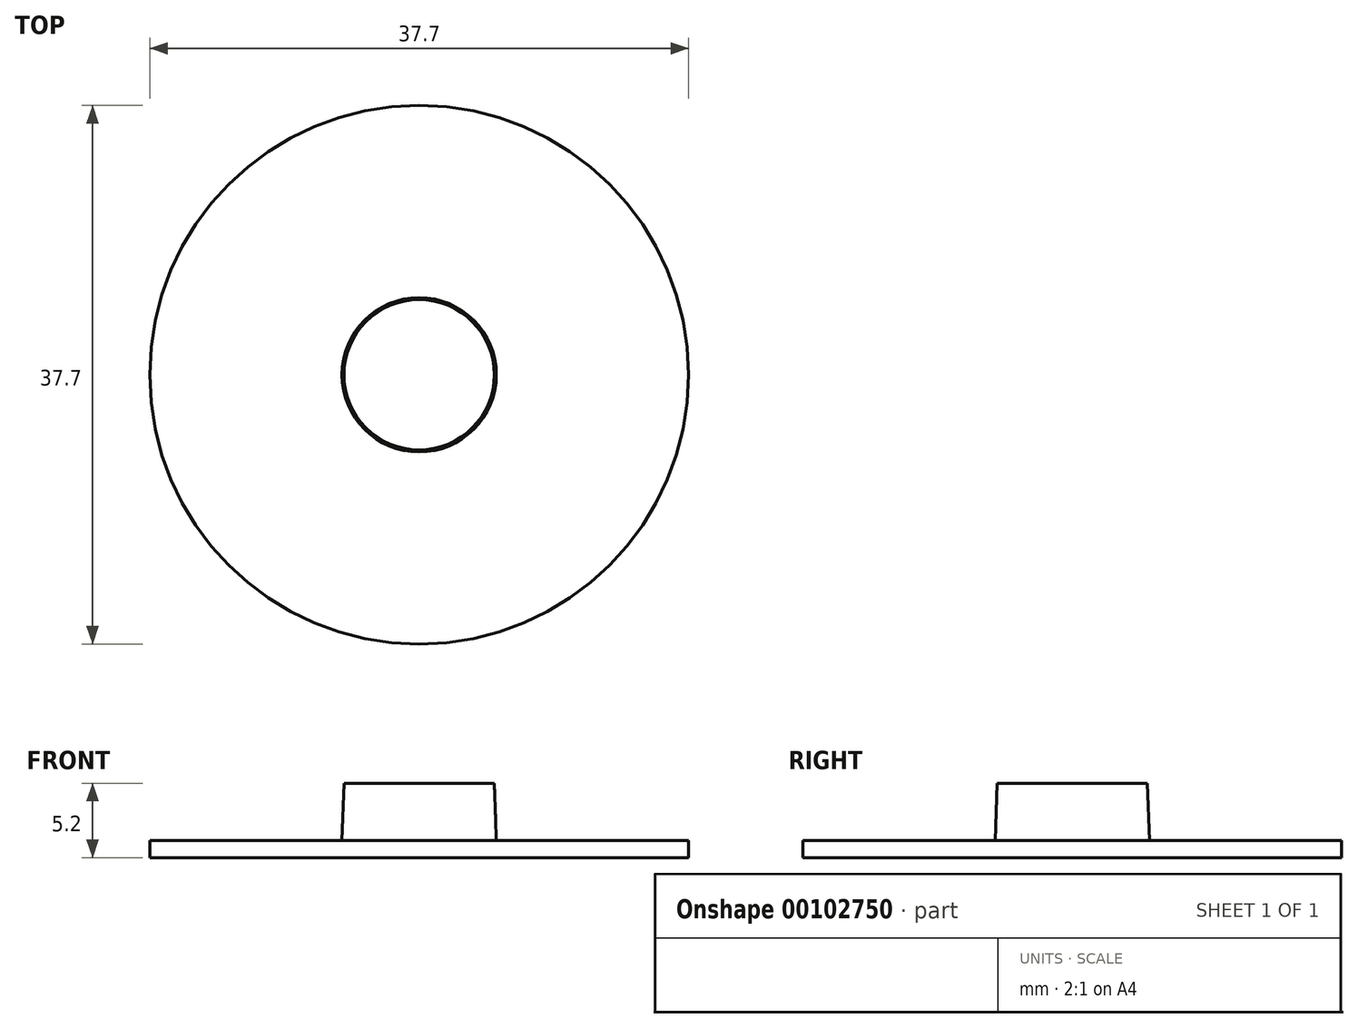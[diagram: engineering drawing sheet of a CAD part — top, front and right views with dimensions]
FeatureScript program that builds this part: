
annotation { "Feature Type Name" : "Feature", "Feature Type Description" : "" }
export const myFeature = defineFeature(function(context is Context, id is Id, definition is map)
    precondition{}
    {
        {
            var Q0;
            Q0=qCreatedBy(makeId("Top.planeOp"),FACE);
            var sketch = newSketch(context, id + "F0", { "sketchPlane" : qUnion([Q0])});
            skCircle(sketch, "E0", {"center": v(0, 0) * mm, "radius": 18.85 * mm});
            skSolve(sketch);
        }
        {
            var Q0;
            Q0 = qSketchRegion(id + "F0", true);
            extrude(context, id + "F1", {"entities" : qUnion([Q0]), "depth" : 1.2 * mm});
        }
        {
            var Q0;
            Q0=makeQuery(id+"F1.opExtrude","CAP_FACE",FACE,{"disambiguationData":[OSD([sQuery(id+"F0.wireOp",EDGE,"E0")])],"isStart":false});
            var sketch = newSketch(context, id + "F2", { "sketchPlane" : qUnion([Q0])});
            skCircle(sketch, "E1", {"center": v(0, 0) * mm, "radius": 5.4 * mm});
            skSolve(sketch);
        }
        {
            var Q0;
            Q0 = qSketchRegion(id + "F2", true);
            extrude(context, id + "F3", {"entities" : qUnion([Q0]), "operationType" : NewBodyOperationType.ADD, "depth" : 4 * mm, "hasDraft" : true, "draftAngle" : 2 * degree, "draftPullDirection" : true});
        }
    });
